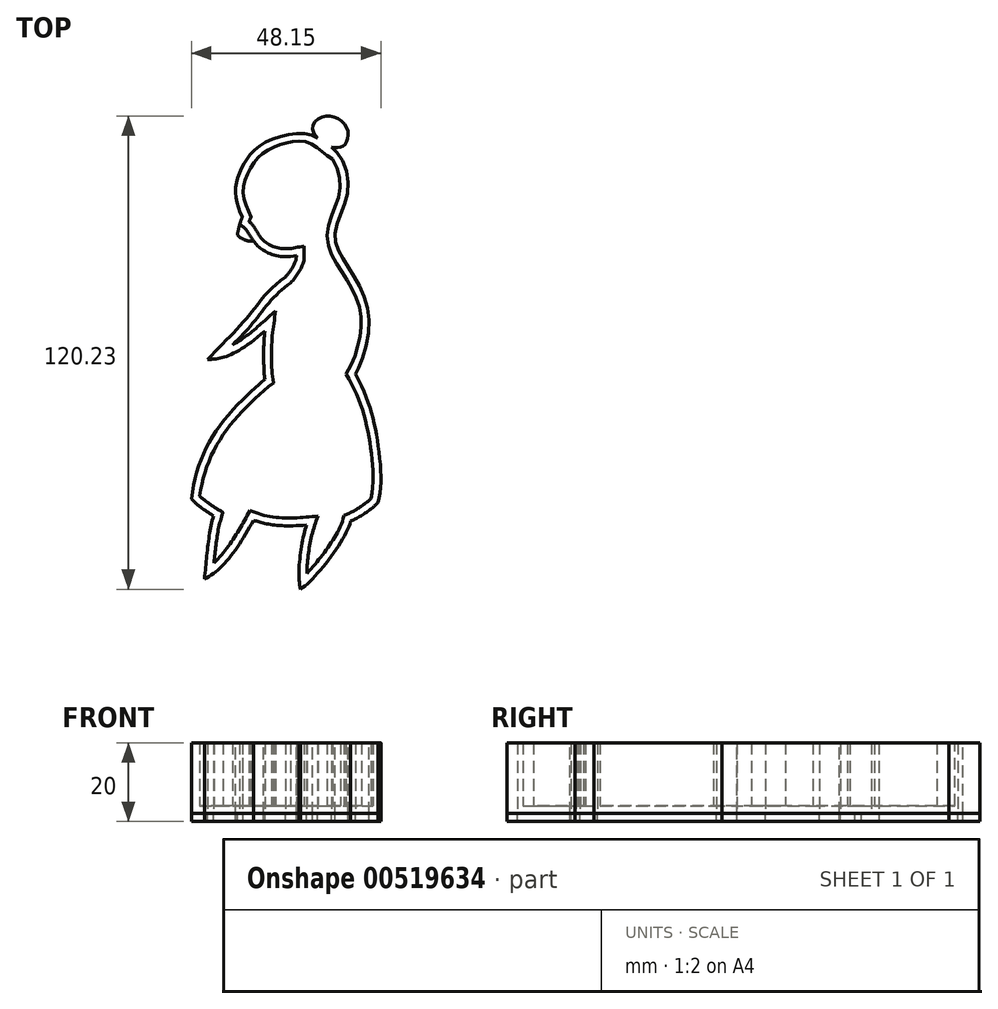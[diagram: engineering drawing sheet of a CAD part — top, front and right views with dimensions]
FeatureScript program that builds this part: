
annotation { "Feature Type Name" : "Feature", "Feature Type Description" : "" }
export const myFeature = defineFeature(function(context is Context, id is Id, definition is map)
    precondition{}
    {
        {
            var Q0;
            Q0=qCreatedBy(makeId("Top.planeOp"),FACE);
            var sketch = newSketch(context, id + "F0", { "sketchPlane" : qUnion([Q0])});
            skFitSpline(sketch, "E0", {"points": [v(2.3, 53.31) * mm, v(3.5, 58.74) * mm, v(9.6, 56.41) * mm, v(9.2, 51.62) * mm, v(5.88, 51.08) * mm], "startDerivative": vector(-26.26, 27.7) * mm, "endDerivative": vector(-18.12, 1.64) * mm});
            skFitSpline(sketch, "E1", {"points": [v(5.88, 51.08) * mm, v(10.15, 41.2) * mm, v(6.8, 29.11) * mm, v(10.23, 20.45) * mm, v(15.47, 6.87) * mm, v(11.96, -6.62) * mm, v(11.22, -7.45) * mm], "startDerivative": vector(35.91, -21.7) * mm, "endDerivative": vector(-10, -8.77) * mm});
            skFitSpline(sketch, "E2", {"points": [v(-1.97, -61.26) * mm, v(-0.44, -44.93) * mm, v(2.18, -40.75) * mm], "startDerivative": vector(-4.83, 18.16) * mm, "endDerivative": vector(9.11, 9.34) * mm});
            skFitSpline(sketch, "E3", {"points": [v(-0.44, -44.93) * mm, v(-13.89, -43.73) * mm, v(-17.34, -41.96) * mm], "startDerivative": vector(-32.66, -3.15) * mm, "endDerivative": vector(-7.47, 6.81) * mm});
            skFitSpline(sketch, "E4", {"points": [v(-13.89, -43.73) * mm, v(-26.38, -58.58) * mm, v(-35.2, -57.93) * mm], "startDerivative": vector(-18.62, -34.29) * mm, "endDerivative": vector(-21.97, 6.96) * mm});
            skFitSpline(sketch, "E5", {"points": [v(-26.38, -58.58) * mm, v(-24.05, -42.64) * mm, v(-19.83, -35.1) * mm], "startDerivative": vector(3.44, 28.3) * mm, "endDerivative": vector(11.25, 15.77) * mm});
            skFitSpline(sketch, "E6", {"points": [v(-24.05, -42.64) * mm, v(-29.7, -38.26) * mm, v(-33.84, -30.95) * mm], "startDerivative": vector(-12.7, 7.93) * mm, "endDerivative": vector(-6.97, 15.34) * mm});
            skFitSpline(sketch, "E7", {"points": [v(-29.7, -38.26) * mm, v(-22.27, -19.46) * mm, v(-11, -7.97) * mm], "startDerivative": vector(5.16, 40.52) * mm, "endDerivative": vector(14.33, 11.5) * mm});
            skFitSpline(sketch, "E8", {"points": [v(-11, -7.97) * mm, v(-11, 4.4) * mm, v(-10.03, 8.08) * mm], "startDerivative": vector(-2.14, 14.97) * mm, "endDerivative": vector(3.23, 8.75) * mm});
            skFitSpline(sketch, "E9", {"points": [v(-11, 4.4) * mm, v(-25.55, -2.84) * mm, v(-29.7, -2.17) * mm], "startDerivative": vector(-33.75, -29.99) * mm, "endDerivative": vector(-10.67, 4.2) * mm});
            skFitSpline(sketch, "E10", {"points": [v(-25.55, -2.84) * mm, v(-15.19, 8.13) * mm, v(-5.8, 18.1) * mm], "startDerivative": vector(21.69, 23.23) * mm, "endDerivative": vector(31.06, 22.7) * mm});
            skFitSpline(sketch, "E11", {"points": [v(-5.8, 18.1) * mm, v(-3.02, 23.53) * mm, v(-8.75, 29.03) * mm], "startDerivative": vector(4.9, 4.75) * mm, "endDerivative": vector(-15.2, 9.98) * mm});
            skFitSpline(sketch, "E12", {"points": [v(-3.02, 23.53) * mm, v(-13.89, 27.2) * mm, v(-18.46, 31.86) * mm], "startDerivative": vector(-29.6, -5.7) * mm, "endDerivative": vector(-21.36, 8) * mm});
            skFitSpline(sketch, "E13", {"points": [v(-13.89, 27.2) * mm, v(-18.02, 28.77) * mm, v(-21.15, 34.08) * mm], "startDerivative": vector(-10.93, -1.04) * mm, "endDerivative": vector(-4.95, 11.4) * mm});
            skFitSpline(sketch, "E14", {"points": [v(-18.02, 28.77) * mm, v(-16.74, 33.29) * mm, v(-12.94, 39.24) * mm], "startDerivative": vector(1.94, 9.9) * mm, "endDerivative": vector(8.03, 11.01) * mm});
            skFitSpline(sketch, "E15", {"points": [v(-16.74, 33.29) * mm, v(-18.51, 39.54) * mm, v(-16.98, 45.64) * mm, v(-11.29, 52.04) * mm, v(2.3, 53.31) * mm, v(4.22, 33.29) * mm], "startDerivative": vector(-17.22, 37.86) * mm, "endDerivative": vector(-12.23, -93.48) * mm});
            skPoint(sketch, "E16.4.internal.orphan", {"position": v(-7.72, -58.58) * mm});
            skFitSpline(sketch, "E17", {"points": [v(-1.97, -61.26) * mm, v(10.77, -43.96) * mm, v(9.6, -38.82) * mm], "startDerivative": vector(18.21, 12.38) * mm, "endDerivative": vector(-7.4, 13.85) * mm});
            skFitSpline(sketch, "E18", {"points": [v(10.77, -43.96) * mm, v(17.74, -39.17) * mm, v(18.6, -37.62) * mm], "startDerivative": vector(13.03, 5.54) * mm, "endDerivative": vector(1.56, 4.62) * mm});
            skFitSpline(sketch, "E19", {"points": [v(11.96, -6.62) * mm, v(17.47, -22.9) * mm, v(17.74, -39.17) * mm, v(15.86, -43.66) * mm, v(16.23, -44.14) * mm], "startDerivative": vector(26.62, -48.68) * mm, "endDerivative": vector(7.65, -5.37) * mm});
            skSolve(sketch);
        }
        {
            var Q0;
            Q0=makeQuery(id+"F0.imprint","IMPRINT",FACE,{"disambiguationData":[TD([[makeQuery(id+"F0.imprint","IMPRINT",EDGE,{"derivedFrom":sQuery(id+"F0.wireOp",EDGE,"E0")}),-1.0]])]});
            extrude(context, id + "F1", {"entities" : qUnion([Q0]), "depth" : 18 * mm, "offsetDistance" : 25 * mm});
        }
        {
            var Q0;
            Q0=makeQuery(id+"F1.opExtrude","CAP_FACE",FACE,{"disambiguationData":[OSD([sQuery(id+"F0.wireOp",EDGE,"E0"),sQuery(id+"F0.wireOp",EDGE,"E1"),sQuery(id+"F0.wireOp",EDGE,"E2"),sQuery(id+"F0.wireOp",EDGE,"E3"),sQuery(id+"F0.wireOp",EDGE,"E4"),sQuery(id+"F0.wireOp",EDGE,"E5"),sQuery(id+"F0.wireOp",EDGE,"E6"),sQuery(id+"F0.wireOp",EDGE,"E7"),sQuery(id+"F0.wireOp",EDGE,"E8"),sQuery(id+"F0.wireOp",EDGE,"E9"),sQuery(id+"F0.wireOp",EDGE,"E10"),sQuery(id+"F0.wireOp",EDGE,"E11"),sQuery(id+"F0.wireOp",EDGE,"E12"),sQuery(id+"F0.wireOp",EDGE,"E13"),sQuery(id+"F0.wireOp",EDGE,"E14"),sQuery(id+"F0.wireOp",EDGE,"E15"),sQuery(id+"F0.wireOp",EDGE,"E17"),sQuery(id+"F0.wireOp",EDGE,"E18"),sQuery(id+"F0.wireOp",EDGE,"E19")])],"isStart":false});
            shell(context, id + "F2", {"entities" : qUnion([Q0]), "thickness" : 2 * mm});
        }
        {
            var Q0;
            Q0 = qSketchRegion(id + "F0", true);
            extrude(context, id + "F3", {"entities" : qUnion([Q0]), "oppositeDirection" : true, "depth" : 2 * mm, "offsetDistance" : 25 * mm});
        }
    });
